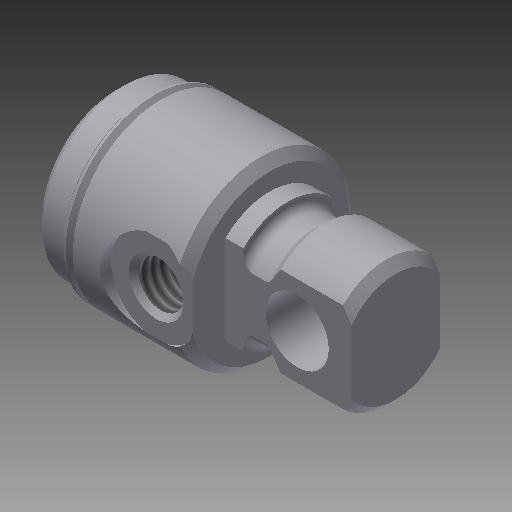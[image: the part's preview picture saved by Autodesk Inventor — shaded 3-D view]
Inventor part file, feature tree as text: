
AUTODESK INVENTOR PART (.ipt)
format: ipt  version: 2018 (Build 220112000, 112)  size: 344,576 bytes
history: native  units: in
note: dims shown in document units (in); Inventor stores cm internally (conversion verified against a paired STEP export)
features: other x154, sketch x7, revolve x4, extrude x2, hole x1, thread x1
ambient origin geometry x8: Origin, YZ Plane, XZ Plane, XY Plane, X Axis, Y Axis, Z Axis, Center Point
bodies: Solid1 (feature_tree)
feature tree (169):
  revolve  "Revolution1"  Angle=360.0deg
  revolve  "Revolution2"  Angle=360.0deg
  extrude  "Extrusion1"  TaperAngle=360.0deg  [1 undecoded]
  hole  "Hole1"  [1 undecoded]
  revolve  "Revolution3"  [1 undecoded]
  thread  "Thread1"  [1 undecoded]
  revolve  "Revolution4"  [1 undecoded]
  extrude  "Extrusion2"  [1 undecoded]
  other  "1_XY"
  other  "1_YZ"
  other  "1_ZX"
  other  "1_X"
  other  "1_Y"
  other  "1_Z"
  other  "1_Center"
  other  "c1_XY"
  other  "c1_YZ"
  other  "c1_ZX"
  other  "c1_X"
  other  "c1_Y"
  other  "c1_Z"
  other  "c1_Center"
  other  "c2_XY"
  other  "c2_YZ"
  other  "c2_ZX"
  other  "c2_X"
  other  "c2_Y"
  other  "c2_Z"
  other  "c2_Center"
  other  "cc1_XY"
  other  "cc1_YZ"
  other  "cc1_ZX"
  other  "cc1_X"
  other  "cc1_Y"
  other  "cc1_Z"
  other  "cc1_Center"
  other  "cc2_XY"
  other  "cc2_YZ"
  other  "cc2_ZX"
  other  "cc2_X"
  other  "cc2_Y"
  other  "cc2_Z"
  other  "cc2_Center"
  other  "lovra1_XY"
  other  "lovra1_YZ"
  other  "lovra1_ZX"
  other  "lovra1_X"
  other  "lovra1_Y"
  other  "lovra1_Z"
  other  "lovra1_Center"
  other  "lovra2_XY"
  other  "lovra2_YZ"
  other  "lovra2_ZX"
  other  "lovra2_X"
  other  "lovra2_Y"
  other  "lovra2_Z"
  other  "lovra2_Center"
  other  "lovra21_XY"
  other  "lovra21_YZ"
  other  "lovra21_ZX"
  other  "lovra21_X"
  other  "lovra21_Y"
  other  "lovra21_Z"
  other  "lovra21_Center"
  other  "lovra22_XY"
  other  "lovra22_YZ"
  other  "lovra22_ZX"
  other  "lovra22_X"
  other  "lovra22_Y"
  other  "lovra22_Z"
  other  "lovra22_Center"
  other  "lovra3_XY"
  other  "lovra3_YZ"
  other  "lovra3_ZX"
  other  "lovra3_X"
  other  "lovra3_Y"
  other  "lovra3_Z"
  other  "lovra3_Center"
  other  "olen_XY"
  other  "olen_YZ"
  other  "olen_ZX"
  other  "olen_X"
  other  "olen_Y"
  other  "olen_Z"
  other  "olen_Center"
  other  "p1_XY"
  other  "p1_YZ"
  other  "p1_ZX"
  other  "p1_X"
  other  "p1_Y"
  other  "p1_Z"
  other  "p1_Center"
  other  "p2_XY"
  other  "p2_YZ"
  other  "p2_ZX"
  other  "p2_X"
  other  "p2_Y"
  other  "p2_Z"
  other  "p2_Center"
  other  "port_XY"
  other  "port_YZ"
  other  "port_ZX"
  other  "port_X"
  other  "port_Y"
  other  "port_Z"
  other  "port_Center"
  other  "port2_XY"
  other  "port2_YZ"
  other  "port2_ZX"
  other  "port2_X"
  other  "port2_Y"
  other  "port2_Z"
  other  "port2_Center"
  other  "thd1_XY"
  other  "thd1_YZ"
  other  "thd1_ZX"
  other  "thd1_X"
  other  "thd1_Y"
  other  "thd1_Z"
  other  "thd1_Center"
  other  "thd2_XY"
  other  "thd2_YZ"
  other  "thd2_ZX"
  other  "thd2_X"
  other  "thd2_Y"
  other  "thd2_Z"
  other  "thd2_Center"
  other  "to_mounting_bracket_XY"
  other  "to_mounting_bracket_YZ"
  other  "to_mounting_bracket_ZX"
  other  "to_mounting_bracket_X"
  other  "to_mounting_bracket_Y"
  other  "to_mounting_bracket_Z"
  other  "to_mounting_bracket_Center"
  other  "to_nut_XY"
  other  "to_nut_YZ"
  other  "to_nut_ZX"
  other  "to_nut_X"
  other  "to_nut_Y"
  other  "to_nut_Z"
  other  "to_nut_Center"
  other  "to_pin_XY"
  other  "to_pin_YZ"
  other  "to_pin_ZX"
  other  "to_pin_X"
  other  "to_pin_Y"
  other  "to_pin_Z"
  other  "to_pin_Center"
  other  "to_screw_XY"
  other  "to_screw_YZ"
  other  "to_screw_ZX"
  other  "to_screw_X"
  other  "to_screw_Y"
  other  "to_screw_Z"
  other  "to_screw_Center"
  other  "to_tube_XY"
  other  "to_tube_YZ"
  other  "to_tube_ZX"
  other  "to_tube_X"
  other  "to_tube_Y"
  other  "to_tube_Z"
  other  "to_tube_Center"
  sketch  "Sketch_18"  dims[d15=0.4605in d16=0.0in]
  sketch  "Sketch_15"  dims[d4=0.154in d5=0.75in d6=0.375in d7=0.25in d8=0.5635in d9=0.484in d10=120.0deg d11=360.0deg]
  sketch  "Sketch_9"  dims[d2=0.437in d3=0.0in]
  sketch  "Sketch4"  dims[d0=360.0deg d1=360.0deg]
  sketch  "Sketch_16"  dims[d12=0.1736in d13=0.0in d14=360.0deg]
  sketch  "Sketch_24"  dims[d17=0.0in d18=0.0in d19=0.0in d20=0.0in d21=0.0in d22=0.0in d23=0.0in]
  sketch  "Sketch_43"
note: 6 required parameter values undecoded (feature->parameter linkage not recoverable at this tier; creation-order binding heuristic only, values carry confidence <= 0.55)
